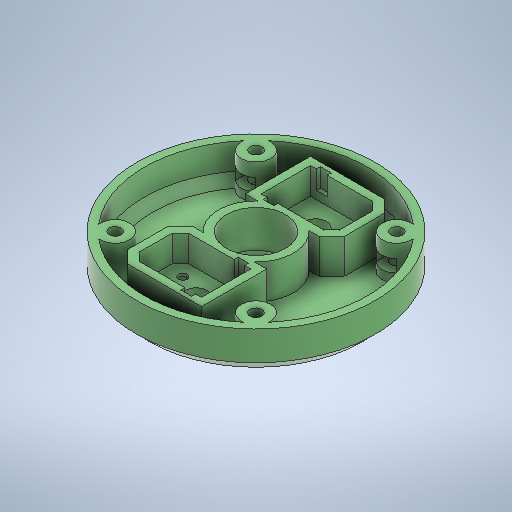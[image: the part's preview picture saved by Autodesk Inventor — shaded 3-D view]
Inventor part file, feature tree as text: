
AUTODESK INVENTOR PART (.ipt)
format: ipt  version: 2025.2 (Build 292293000, 293)  size: 567,808 bytes
history: native  units: mm
features: extrude x8, sketch x3, chamfer x2, shell x1, plane x1, pattern_circular x1
ambient origin geometry x8: Origin, YZ Plane, XZ Plane, XY Plane, X Axis, Y Axis, Z Axis, Center Point
bodies: Solid1 (feature_tree)
feature tree (16):
  sketch  "Sketch1"  dims[d1=18.5mm d2=90.0mm]
  extrude  "General Shape"  Depth=18.5mm
  extrude  "Shaft support Slot"  Depth=16.0mm
  chamfer  "Corners of shaft support slots"  Distance=16.0mm
  extrude  "T3 nut slots"  Depth=45.0mm
  extrude  "Holes for smooth rod & M3 bolt"  Depth=4.5mm
  extrude  "Base for 608 Bearing"  Depth=2.0mm TaperAngle=0.0deg
  chamfer  "Material reduction on the base"  Distance=37.5mm
  shell  "Shell1"  Thickness=9.0mm
  sketch  "Sketch4"  dims[d5=8.0mm d12=22.2mm d14=16.0mm d15=0.0mm]
  extrude  "Slot for M4 fasteners"  Depth=26.5mm
  plane  "Work Plane4"
  extrude  "Slot for M4 nuts to fasen to the swivel base"  Depth=20.0mm
  extrude  "Extrusion13"  Depth=20.0mm
  pattern_circular  "Circular Pattern2"  [2 undecoded]
  sketch  "Sketch6"  dims[d16=10.0mm d17=0.0mm d26=45.0mm d32=4.5mm d42=2.0mm d43=0.0mm d44=37.5mm d50=9.0mm d53=26.5mm d54=15.25mm d55=15.25mm d56=3.3mm d60=5.8mm d61=5.8mm d62=5.0mm d63=0.0mm d64=5.0mm d65=0.0mm d66=3.0mm d67=2.0mm d68=45.0deg d70=5.8mm d71=8.0mm d72=5.8mm d73=6.0mm d74=8.0mm d75=3.0mm d76=45.0deg d77=7.5mm d78=11.0mm d79=5.0mm d80=0.0mm d81=-5.0mm d82=4.7mm d83=0.0mm d84=8.2mm d89=9.0mm d90=9.0mm d91=5.0mm d92=2.0mm d93=45.0deg d94=4.0mm d95=7.0mm d96=21.5mm d97=7.0mm d98=0.0mm d99=20.0mm d100=360.0deg d36=0.5mm d37=0.872665mm d38=0.5mm d39=0.872665mm]
note: 2 required parameter values undecoded (feature->parameter linkage not recoverable at this tier; creation-order binding heuristic only, values carry confidence <= 0.55)
